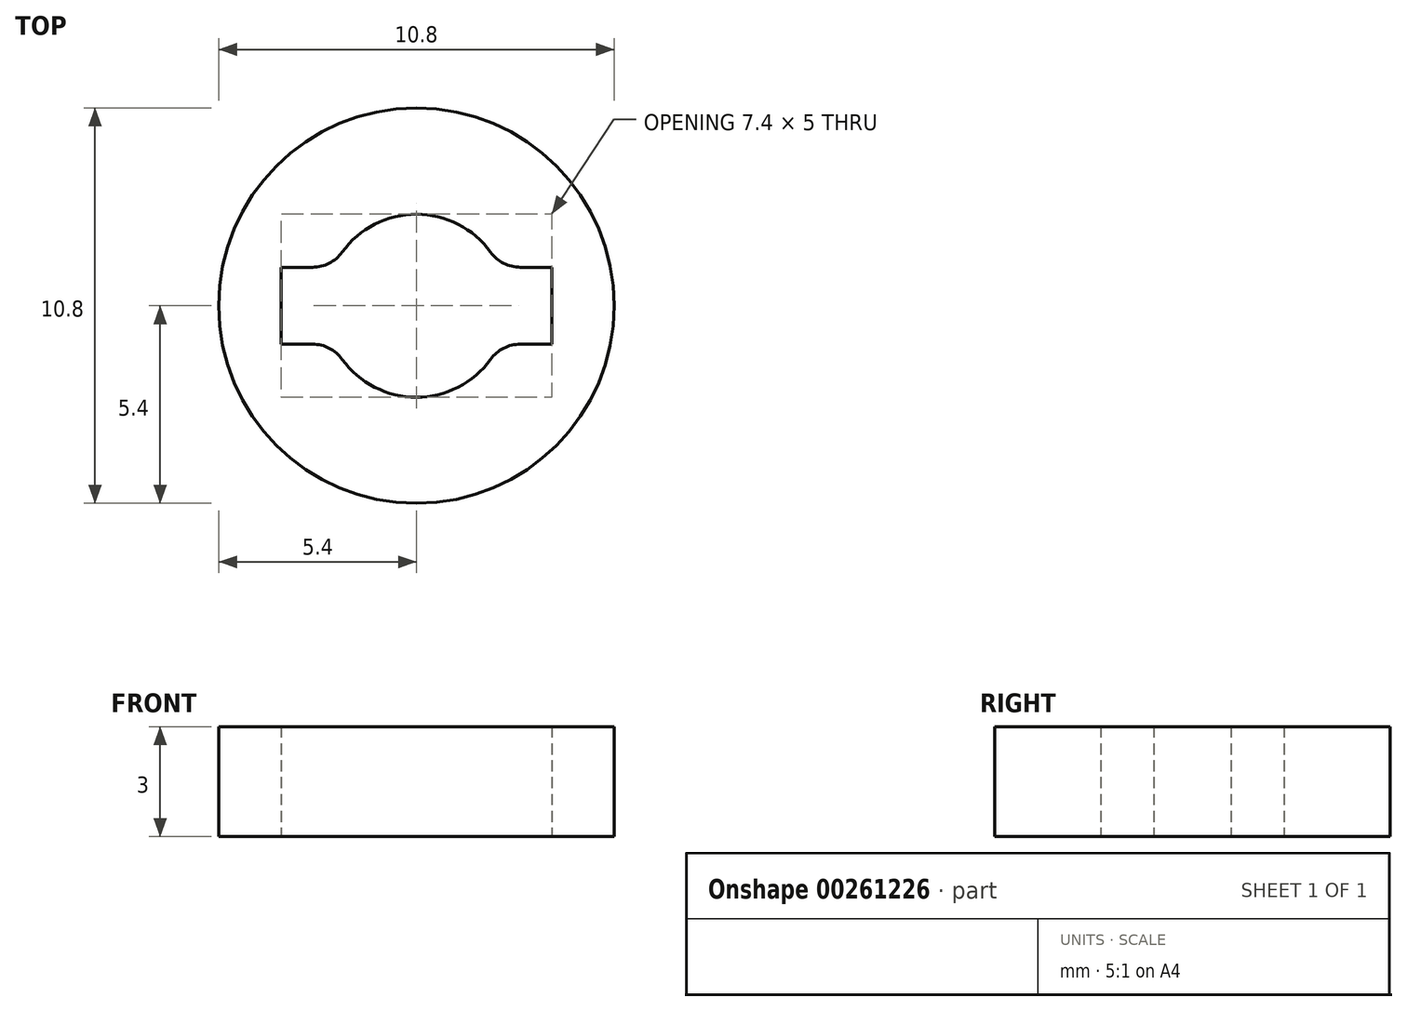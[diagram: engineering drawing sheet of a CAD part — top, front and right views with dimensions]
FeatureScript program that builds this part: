
annotation { "Feature Type Name" : "Feature", "Feature Type Description" : "" }
export const myFeature = defineFeature(function(context is Context, id is Id, definition is map)
    precondition{}
    {
        {
            var Q0;
            Q0=qCreatedBy(makeId("Top.planeOp"),FACE);
            var sketch = newSketch(context, id + "F0", { "sketchPlane" : qUnion([Q0])});
            skCircle(sketch, "E0", {"center": v(0, 0) * mm, "radius": 5.4 * mm});
            skArc(sketch, "E1", {"start": v(2.03, 1.46) * mm, "mid": v(0, 2.5) * mm, "end": v(-2.03, 1.46) * mm});
            skLineSegment(sketch, "E2", {"start": v(0, 0) * mm, "end": v(0, 0) * mm});
            skLineSegment(sketch, "E3", {"start": v(0, 0) * mm, "end": v(0, 6.9) * mm, "construction": true});
            skLineSegment(sketch, "E4", {"start": v(3.7, 1.05) * mm, "end": v(3.7, -1.05) * mm});
            skLineSegment(sketch, "E5", {"start": v(2.84, 1.05) * mm, "end": v(3.7, 1.05) * mm});
            skLineSegment(sketch, "E6", {"start": v(2.84, -1.05) * mm, "end": v(3.7, -1.05) * mm});
            skLineSegment(sketch, "E7", {"start": v(0, 0) * mm, "end": v(1.43, 0) * mm, "construction": true});
            skLineSegment(sketch, "E8", {"start": v(2.5, 0) * mm, "end": v(2.5, 2.48) * mm, "construction": true});
            skPoint(sketch, "E9.orphan", {"position": v(3.7, 1.31) * mm});
            skPoint(sketch, "E10.orphan", {"position": v(3.7, -1.15) * mm});
            skLineSegment(sketch, "E11.MirrorCS", {"start": v(-2.84, 1.05) * mm, "end": v(-3.7, 1.05) * mm});
            skLineSegment(sketch, "E12.MirrorCS", {"start": v(-3.7, 1.05) * mm, "end": v(-3.7, -1.05) * mm});
            skLineSegment(sketch, "E13.MirrorCS", {"start": v(-2.84, -1.05) * mm, "end": v(-3.7, -1.05) * mm});
            skArc(sketch, "E14.trimOffspring", {"start": v(-2.03, -1.46) * mm, "mid": v(0, -2.5) * mm, "end": v(2.03, -1.46) * mm});
            skArc(sketch, "E15", {"start": v(2.84, -1.05) * mm, "mid": v(2.38, -1.16) * mm, "end": v(2.03, -1.46) * mm});
            skPoint(sketch, "E16.orphan", {"position": v(2.27, -1.05) * mm});
            skArc(sketch, "E17.MirrorCS", {"start": v(2.84, 1.05) * mm, "mid": v(2.38, 1.16) * mm, "end": v(2.03, 1.46) * mm});
            skArc(sketch, "E18.MirrorCS", {"start": v(-2.84, -1.05) * mm, "mid": v(-2.38, -1.16) * mm, "end": v(-2.03, -1.46) * mm});
            skArc(sketch, "E19.MirrorCS", {"start": v(-2.84, 1.05) * mm, "mid": v(-2.38, 1.16) * mm, "end": v(-2.03, 1.46) * mm});
            skPoint(sketch, "E20.orphan", {"position": v(2.27, 1.05) * mm});
            skPoint(sketch, "E21.orphan", {"position": v(-2.27, 1.05) * mm});
            skPoint(sketch, "E22.orphan", {"position": v(-2.27, -1.05) * mm});
            skSolve(sketch);
        }
        {
            var Q0;
            Q0=makeQuery(id+"F0.imprint","IMPRINT",FACE,{"disambiguationData":[TD([[makeQuery(id+"F0.imprint","IMPRINT",EDGE,{"derivedFrom":sQuery(id+"F0.wireOp",EDGE,"E0")}),1.0]])]});
            extrude(context, id + "F1", {"entities" : qUnion([Q0]), "depth" : 3 * mm});
        }
    });
